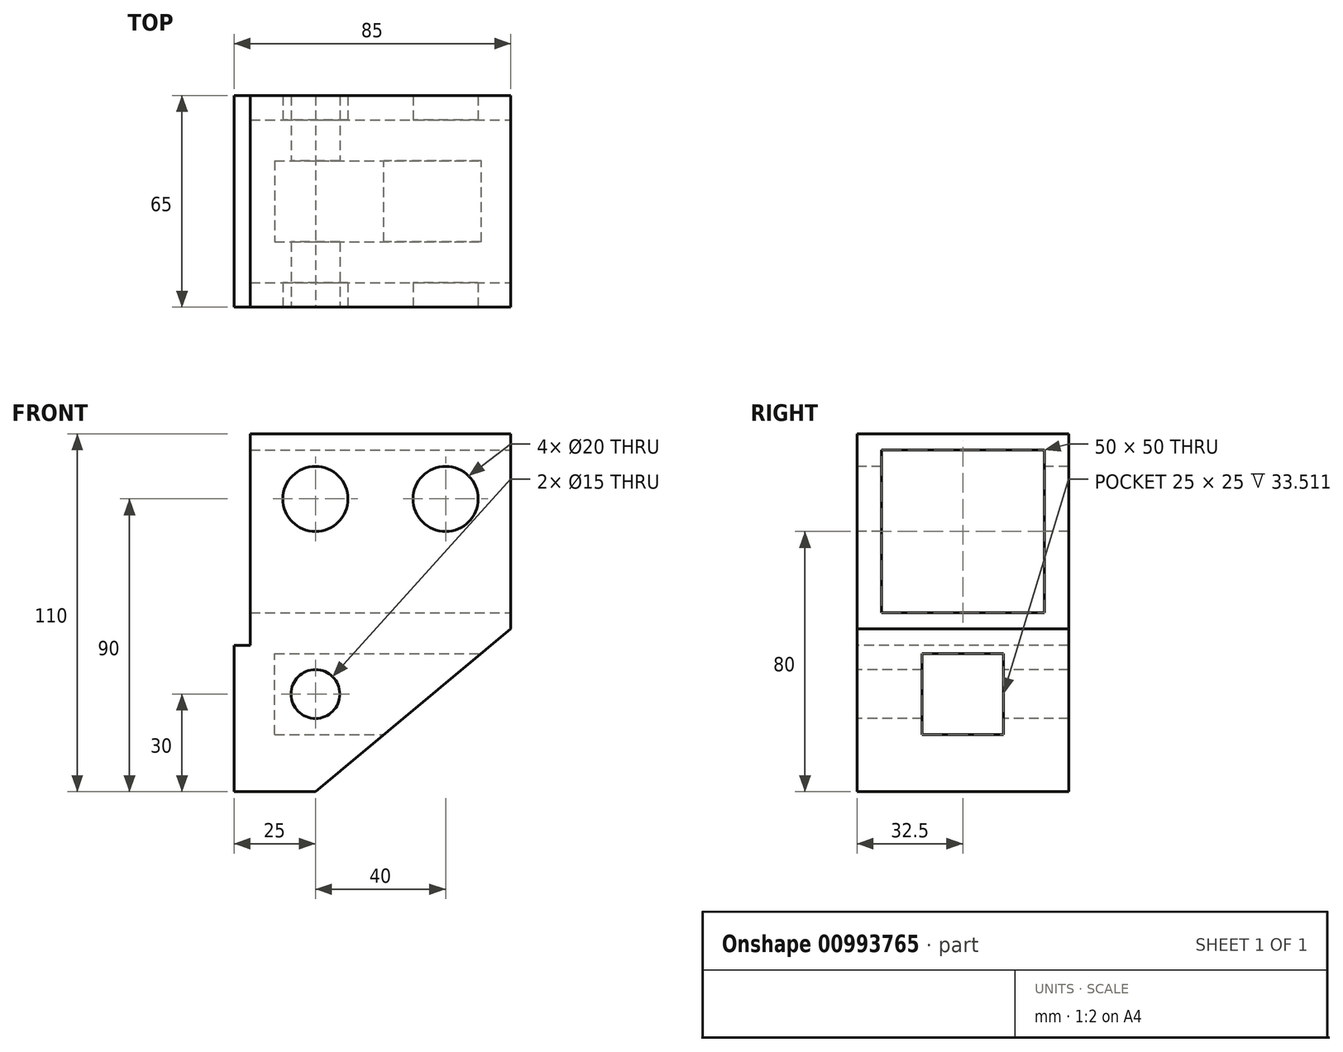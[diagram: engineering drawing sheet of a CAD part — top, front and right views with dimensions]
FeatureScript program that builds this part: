
annotation { "Feature Type Name" : "Feature", "Feature Type Description" : "" }
export const myFeature = defineFeature(function(context is Context, id is Id, definition is map)
    precondition{}
    {
        {
            var Q0;
            Q0=qCreatedBy(makeId("Right.planeOp"),FACE);
            var sketch = newSketch(context, id + "F0", { "sketchPlane" : qUnion([Q0])});
            skLineSegment(sketch, "E0.bottom", {"start": v(-32.5, 55) * mm, "end": v(32.5, 55) * mm});
            skLineSegment(sketch, "E0.top", {"start": v(-32.5, -55) * mm, "end": v(32.5, -55) * mm});
            skLineSegment(sketch, "E0.left", {"start": v(-32.5, 55) * mm, "end": v(-32.5, -55) * mm});
            skLineSegment(sketch, "E0.right", {"start": v(32.5, 55) * mm, "end": v(32.5, -55) * mm});
            skPoint(sketch, "E0.middle", {"position": v(0, 0) * mm});
            skSolve(sketch);
        }
        {
            var Q0;
            Q0=makeQuery(id+"F0.imprint","IMPRINT",FACE,{"disambiguationData":[TD([[makeQuery(id+"F0.imprint","IMPRINT",EDGE,{"derivedFrom":sQuery(id+"F0.wireOp",EDGE,"E0.bottom")}),-1.0]])]});
            extrude(context, id + "F1", {"entities" : qUnion([Q0]), "endBound" : BoundingType.SYMMETRIC, "depth" : 80 * mm, "offsetDistance" : 25 * mm});
        }
        {
            var Q0;
            Q0=makeQuery(id+"F1.opExtrude","CAP_EDGE",EDGE,{"disambiguationData":[OSD([sQuery(id+"F0.wireOp",EDGE,"E0.top")])],"isStart":false});
            chamfer(context, id + "F2", {"entities" : qUnion([Q0]), "chamferType" : ChamferType.TWO_OFFSETS, "width1" : 50 * mm, "oppositeDirection" : false, "width2" : 60 * mm, "tangentPropagation" : true});
        }
        {
            var Q0;
            Q0=makeQuery(id+"F1.opExtrude","SWEPT_FACE",FACE,{"disambiguationData":[OSD([sQuery(id+"F0.wireOp",EDGE,"E0.left")])]});
            var sketch = newSketch(context, id + "F3", { "sketchPlane" : qUnion([Q0])});
            skCircle(sketch, "E1", {"center": v(-20, 35) * mm, "radius": 10 * mm});
            skCircle(sketch, "E2", {"center": v(20, 35) * mm, "radius": 10 * mm});
            skCircle(sketch, "E3", {"center": v(-20, -25) * mm, "radius": 7.5 * mm});
            skSolve(sketch);
        }
        {
            var Q0;
            Q0 = qSketchRegion(id + "F3", true);
            extrude(context, id + "F4", {"entities" : qUnion([Q0]), "operationType" : NewBodyOperationType.REMOVE, "endBound" : BoundingType.UP_TO_NEXT, "oppositeDirection" : true, "depth" : 25 * mm, "offsetDistance" : 25 * mm});
        }
        {
            var Q0;
            Q0=makeQuery(id+"F1.opExtrude","CAP_FACE",FACE,{"disambiguationData":[OSD([sQuery(id+"F0.wireOp",EDGE,"E0.bottom"),sQuery(id+"F0.wireOp",EDGE,"E0.top"),sQuery(id+"F0.wireOp",EDGE,"E0.left"),sQuery(id+"F0.wireOp",EDGE,"E0.right")])],"isStart":false});
            var sketch = newSketch(context, id + "F5", { "sketchPlane" : qUnion([Q0])});
            skLineSegment(sketch, "E4.bottom", {"start": v(-25, 50) * mm, "end": v(25, 50) * mm});
            skLineSegment(sketch, "E4.top", {"start": v(-25, 0) * mm, "end": v(25, 0) * mm});
            skLineSegment(sketch, "E4.left", {"start": v(-25, 50) * mm, "end": v(-25, 0) * mm});
            skLineSegment(sketch, "E4.right", {"start": v(25, 50) * mm, "end": v(25, 0) * mm});
            skPoint(sketch, "E4.middle", {"position": v(0, 25) * mm});
            skSolve(sketch);
        }
        {
            var Q0;
            Q0=makeQuery(id+"F5.imprint","IMPRINT",FACE,{"disambiguationData":[TD([[makeQuery(id+"F5.imprint","IMPRINT",EDGE,{"derivedFrom":sQuery(id+"F5.wireOp",EDGE,"E4.bottom")}),-1.0]])]});
            var Q1;
            Q1=makeQuery(id+"F1.opExtrude","CAP_FACE",FACE,{"disambiguationData":[OSD([sQuery(id+"F0.wireOp",EDGE,"E0.bottom"),sQuery(id+"F0.wireOp",EDGE,"E0.top"),sQuery(id+"F0.wireOp",EDGE,"E0.left"),sQuery(id+"F0.wireOp",EDGE,"E0.right")])],"isStart":true});
            extrude(context, id + "F6", {"entities" : qUnion([Q0]), "operationType" : NewBodyOperationType.REMOVE, "endBound" : BoundingType.UP_TO_SURFACE, "oppositeDirection" : true, "depth" : 25 * mm, "endBoundEntityFace" : qUnion([Q1]), "offsetDistance" : 25 * mm});
        }
        {
            var Q0;
            Q0=makeQuery(id+"F1.opExtrude","CAP_FACE",FACE,{"disambiguationData":[OSD([sQuery(id+"F0.wireOp",EDGE,"E0.bottom"),sQuery(id+"F0.wireOp",EDGE,"E0.top"),sQuery(id+"F0.wireOp",EDGE,"E0.left"),sQuery(id+"F0.wireOp",EDGE,"E0.right")])],"isStart":true});
            extrude(context, id + "F7", {"entities" : qUnion([Q0]), "operationType" : NewBodyOperationType.ADD, "depth" : 5 * mm, "offsetDistance" : 25 * mm});
        }
        {
            var Q0;
            Q0=makeQuery(id+"F7.opExtrude","CAP_FACE",FACE,{"disambiguationData":[OSD([sQuery(id+"F0.wireOp",EDGE,"E0.bottom"),sQuery(id+"F0.wireOp",EDGE,"E0.top"),sQuery(id+"F0.wireOp",EDGE,"E0.left"),sQuery(id+"F0.wireOp",EDGE,"E0.right")])],"isStart":false});
            var sketch = newSketch(context, id + "F8", { "sketchPlane" : qUnion([Q0])});
            skLineSegment(sketch, "E5.bottom", {"start": v(-32.5, 55) * mm, "end": v(32.5, 55) * mm});
            skLineSegment(sketch, "E5.top", {"start": v(-32.5, -10) * mm, "end": v(32.5, -10) * mm});
            skLineSegment(sketch, "E5.left", {"start": v(-32.5, 55) * mm, "end": v(-32.5, -10) * mm});
            skLineSegment(sketch, "E5.right", {"start": v(32.5, 55) * mm, "end": v(32.5, -10) * mm});
            skSolve(sketch);
        }
        {
            var Q0;
            Q0=makeQuery(id+"F8.imprint","IMPRINT",FACE,{"disambiguationData":[TD([[makeQuery(id+"F8.imprint","IMPRINT",EDGE,{"derivedFrom":sQuery(id+"F8.wireOp",EDGE,"E5.bottom")}),1.0]])]});
            extrude(context, id + "F9", {"entities" : qUnion([Q0]), "operationType" : NewBodyOperationType.REMOVE, "oppositeDirection" : true, "depth" : 5 * mm, "offsetDistance" : 25 * mm});
        }
        {
            var Q0;
            Q0=qCreatedBy(makeId("Front.planeOp"),FACE);
            var sketch = newSketch(context, id + "F10", { "sketchPlane" : qUnion([Q0])});
            skLineSegment(sketch, "E6", {"start": v(-32.52, -25) * mm, "end": v(-32.52, -12.5) * mm});
            skLineSegment(sketch, "E7.bottom", {"start": v(-32.52, -12.5) * mm, "end": v(33.28, -12.5) * mm});
            skLineSegment(sketch, "E7.top", {"start": v(-32.52, -37.5) * mm, "end": v(33.28, -37.5) * mm});
            skLineSegment(sketch, "E7.left", {"start": v(-32.52, -12.5) * mm, "end": v(-32.52, -37.5) * mm});
            skLineSegment(sketch, "E7.right", {"start": v(33.28, -12.5) * mm, "end": v(33.28, -37.5) * mm});
            skSolve(sketch);
        }
        {
            var Q0;
            Q0 = qSketchRegion(id + "F10", true);
            extrude(context, id + "F11", {"entities" : qUnion([Q0]), "operationType" : NewBodyOperationType.REMOVE, "endBound" : BoundingType.SYMMETRIC, "oppositeDirection" : true, "depth" : 25 * mm, "offsetDistance" : 25 * mm});
        }
    });
